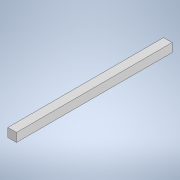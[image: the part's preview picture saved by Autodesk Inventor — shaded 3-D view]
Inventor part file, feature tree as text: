
AUTODESK INVENTOR PART (.ipt)
format: ipt  version: 2020 (Build 240168000, 168)  size: 99,328 bytes
history: native  units: mm
features: other x1, extrude x1, sketch x1
ambient origin geometry x8: Origin, YZ Plane, XZ Plane, XY Plane, X Axis, Y Axis, Z Axis, Center Point
bodies: Solid1 (feature_tree)
feature tree (3):
  other  "<userpath>\Documents\Development\paragon-printer\Paragon Printer Parameters.xlsx"
  extrude  "Extrusion1"  Depth=20.0mm
  sketch  "Sketch1"  dims[d0=20.0mm d1=20.0mm d2=360.0mm d3=0.0mm]
